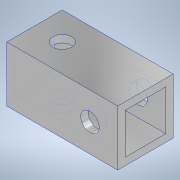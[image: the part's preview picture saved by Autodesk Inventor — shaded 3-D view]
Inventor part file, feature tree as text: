
AUTODESK INVENTOR PART (.ipt)
format: ipt  version: 2020.3 (Build 243373000, 373)  size: 123,392 bytes
history: native  units: mm
features: sketch x3, hole x2, other x1, extrude x1
ambient origin geometry x8: Origin, YZ Plane, XZ Plane, XY Plane, X Axis, Y Axis, Z Axis, Center Point
bodies: Body1 (feature_tree)
feature tree (7):
  other  "ソリッド1"
  extrude  "押し出し1"  Depth=9.0mm
  hole  "穴1"  [1 undecoded]
  hole  "穴2"  [1 undecoded]
  sketch  "スケッチ1"
  sketch  "スケッチ2"
  sketch  "スケッチ3"
note: 2 required parameter values undecoded (feature->parameter linkage not recoverable at this tier; creation-order binding heuristic only, values carry confidence <= 0.55)
